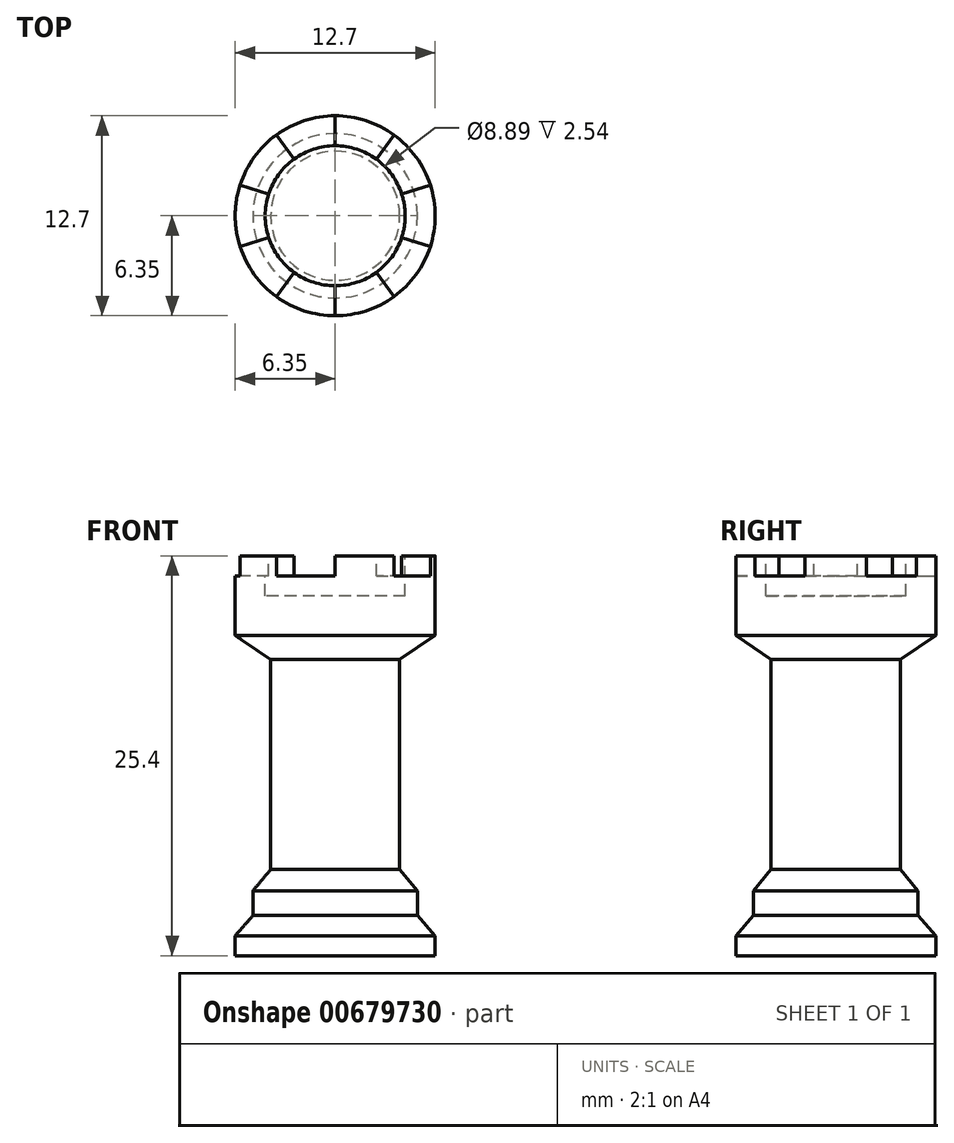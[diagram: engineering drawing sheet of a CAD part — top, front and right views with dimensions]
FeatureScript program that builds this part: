
annotation { "Feature Type Name" : "Feature", "Feature Type Description" : "" }
export const myFeature = defineFeature(function(context is Context, id is Id, definition is map)
    precondition{}
    {
        {
            var Q0;
            Q0=qCreatedBy(makeId("Front.planeOp"),FACE);
            var sketch = newSketch(context, id + "F0", { "sketchPlane" : qUnion([Q0])});
            skLineSegment(sketch, "E0", {"start": v(-6.35, 0) * mm, "end": v(6.35, 0) * mm});
            skLineSegment(sketch, "E1", {"start": v(-6.35, 0) * mm, "end": v(-6.35, 1.27) * mm});
            skLineSegment(sketch, "E2", {"start": v(6.35, 0) * mm, "end": v(6.35, 1.27) * mm});
            skLineSegment(sketch, "E3", {"start": v(-4.1, 3.83) * mm, "end": v(4.1, 3.83) * mm, "construction": true});
            skLineSegment(sketch, "E4", {"start": v(0, 0) * mm, "end": v(0, 25.4) * mm});
            skPoint(sketch, "E5", {"position": v(0, 3.83) * mm});
            skLineSegment(sketch, "E6", {"start": v(-6.35, 25.4) * mm, "end": v(6.35, 25.4) * mm});
            skLineSegment(sketch, "E7", {"start": v(6.35, 25.4) * mm, "end": v(6.35, 20.34) * mm});
            skLineSegment(sketch, "E8", {"start": v(-4.1, 20.34) * mm, "end": v(-4.1, 5.47) * mm});
            skLineSegment(sketch, "E9", {"start": v(4.1, 3.83) * mm, "end": v(4.1, 5.47) * mm, "construction": true});
            skPoint(sketch, "E10", {"position": v(0, 20.34) * mm});
            skLineSegment(sketch, "E11", {"start": v(4.1, 3.83) * mm, "end": v(5.22, 2.55) * mm, "construction": true});
            skLineSegment(sketch, "E12", {"start": v(-4.1, 3.83) * mm, "end": v(-5.22, 2.55) * mm, "construction": true});
            skLineSegment(sketch, "E13", {"start": v(6.35, 20.34) * mm, "end": v(4.1, 18.8) * mm});
            skLineSegment(sketch, "E14", {"start": v(-6.35, 20.34) * mm, "end": v(-4.1, 18.8) * mm});
            skLineSegment(sketch, "E15", {"start": v(-4.1, 18.8) * mm, "end": v(4.1, 18.8) * mm, "construction": true});
            skLineSegment(sketch, "E16", {"start": v(-5.22, 2.55) * mm, "end": v(-5.22, 4.13) * mm});
            skLineSegment(sketch, "E17", {"start": v(5.22, 2.55) * mm, "end": v(5.22, 4.13) * mm});
            skLineSegment(sketch, "E18", {"start": v(5.22, 4.13) * mm, "end": v(4.1, 5.47) * mm});
            skLineSegment(sketch, "E19", {"start": v(-5.22, 4.13) * mm, "end": v(-4.1, 5.47) * mm});
            skLineSegment(sketch, "E20", {"start": v(-4.1, 5.47) * mm, "end": v(4.1, 5.47) * mm, "construction": true});
            skLineSegment(sketch, "E21", {"start": v(-5.22, 4.13) * mm, "end": v(5.22, 4.13) * mm, "construction": true});
            skLineSegment(sketch, "E22", {"start": v(-5.22, 2.55) * mm, "end": v(-6.35, 1.27) * mm});
            skLineSegment(sketch, "E23", {"start": v(5.22, 2.55) * mm, "end": v(6.35, 1.27) * mm});
            skLineSegment(sketch, "E24", {"start": v(-4.1, 5.47) * mm, "end": v(-4.1, 3.83) * mm, "construction": true});
            skLineSegment(sketch, "E25", {"start": v(4.1, 5.47) * mm, "end": v(4.1, 20.34) * mm});
            skLineSegment(sketch, "E26", {"start": v(-6.35, 20.34) * mm, "end": v(6.35, 20.34) * mm, "construction": true});
            skLineSegment(sketch, "E27", {"start": v(-6.35, 20.34) * mm, "end": v(-6.35, 25.4) * mm});
            skSolve(sketch);
        }
        {
            var Q0;
            {var subQ1=sQuery(id+"F0.wireOp",EDGE,"E2");Q0=makeQuery(id+"F0.imprint","IMPRINT",FACE,{"disambiguationData":[TD([[makeQuery(id+"F0.imprint","IMPRINT",EDGE,{"derivedFrom":subQ1}),1.0]])]});}
            var Q1;
            Q1=sQuery(id+"F0.wireOp",EDGE,"E4");
            revolve(context, id + "F1", {"entities" : qUnion([Q0]), "axis" : qUnion([Q1]), "revolveType" : RevolveType.FULL});
        }
        {
            var Q0;
            Q0=makeQuery(id+"F1.opRevolve","SWEPT_FACE",FACE,{"disambiguationData":[OSD([sQuery(id+"F0.wireOp",EDGE,"E6")])]});
            var sketch = newSketch(context, id + "F2", { "sketchPlane" : qUnion([Q0])});
            skCircle(sketch, "E28", {"center": v(0, 0) * mm, "radius": 4.45 * mm});
            skLineSegment(sketch, "E29", {"start": v(0, 4.45) * mm, "end": v(0, 6.35) * mm});
            skLineSegment(sketch, "E30.1.0", {"start": v(-2.61, 3.6) * mm, "end": v(-3.73, 5.14) * mm});
            skLineSegment(sketch, "E30.2.0", {"start": v(-4.23, 1.37) * mm, "end": v(-6.04, 1.96) * mm});
            skLineSegment(sketch, "E30.3.0", {"start": v(-4.23, -1.37) * mm, "end": v(-6.04, -1.96) * mm});
            skLineSegment(sketch, "E30.4.0", {"start": v(-2.61, -3.6) * mm, "end": v(-3.73, -5.14) * mm});
            skLineSegment(sketch, "E30.5.0", {"start": v(0, -4.45) * mm, "end": v(0, -6.35) * mm});
            skLineSegment(sketch, "E30.6.0", {"start": v(2.61, -3.6) * mm, "end": v(3.73, -5.14) * mm});
            skLineSegment(sketch, "E30.7.0", {"start": v(4.23, -1.37) * mm, "end": v(6.04, -1.96) * mm});
            skLineSegment(sketch, "E30.8.0", {"start": v(4.23, 1.37) * mm, "end": v(6.04, 1.96) * mm});
            skLineSegment(sketch, "E30.9.0", {"start": v(2.61, 3.6) * mm, "end": v(3.73, 5.14) * mm});
            skSolve(sketch);
        }
        {
            var Q0;
            {var subQ0=sQuery(id+"F2.wireOp",EDGE,"E28");var subQ5=makeQuery(id+"F2.imprint","INTERSECT",VERTEX,{"derivedFrom":[subQ0,sQuery(id+"F2.wireOp",EDGE,"E30.8.0")]});Q0=makeQuery(id+"F2.imprint","IMPRINT",FACE,{"disambiguationData":[TD([[makeQuery(id+"F2.imprint","IMPRINT",EDGE,{"disambiguationData":[TD([[subQ5,-1.0]])],"derivedFrom":subQ0}),1.0]])]});}
            var Q1;
            {var subQ0=sQuery(id+"F2.wireOp",EDGE,"E29");Q1=makeQuery(id+"F2.imprint","IMPRINT",FACE,{"disambiguationData":[TD([[makeQuery(id+"F2.imprint","IMPRINT",EDGE,{"derivedFrom":subQ0}),1.0]])]});}
            var Q2;
            {var subQ0=sQuery(id+"F2.wireOp",EDGE,"E30.8.0");Q2=makeQuery(id+"F2.imprint","IMPRINT",FACE,{"disambiguationData":[TD([[makeQuery(id+"F2.imprint","IMPRINT",EDGE,{"derivedFrom":subQ0}),1.0]])]});}
            var Q3;
            {var subQ0=sQuery(id+"F2.wireOp",EDGE,"E30.6.0");Q3=makeQuery(id+"F2.imprint","IMPRINT",FACE,{"disambiguationData":[TD([[makeQuery(id+"F2.imprint","IMPRINT",EDGE,{"derivedFrom":subQ0}),1.0]])]});}
            var Q4;
            {var subQ0=sQuery(id+"F2.wireOp",EDGE,"E30.4.0");Q4=makeQuery(id+"F2.imprint","IMPRINT",FACE,{"disambiguationData":[TD([[makeQuery(id+"F2.imprint","IMPRINT",EDGE,{"derivedFrom":subQ0}),1.0]])]});}
            var Q5;
            {var subQ0=sQuery(id+"F2.wireOp",EDGE,"E30.2.0");Q5=makeQuery(id+"F2.imprint","IMPRINT",FACE,{"disambiguationData":[TD([[makeQuery(id+"F2.imprint","IMPRINT",EDGE,{"derivedFrom":subQ0}),1.0]])]});}
            extrude(context, id + "F3", {"entities" : qUnion([Q0, Q1, Q2, Q3, Q4, Q5]), "operationType" : NewBodyOperationType.REMOVE, "oppositeDirection" : true, "depth" : 1.27 * mm, "offsetDistance" : 25.4 * mm});
        }
        {
            var Q0;
            Q0=makeQuery(id+"F3.boolean.opBoolean","COPY",FACE,{"derivedFrom":makeQuery(id+"F3.opExtrude","CAP_FACE",FACE,{"disambiguationData":[OSD([sQuery(id+"F0.wireOp",EDGE,"E6"),sQuery(id+"F0.wireOp",EDGE,"E7"),sQuery(id+"F2.wireOp",EDGE,"E28"),sQuery(id+"F2.wireOp",EDGE,"E29"),sQuery(id+"F2.wireOp",EDGE,"E30.1.0"),sQuery(id+"F2.wireOp",EDGE,"E30.2.0"),sQuery(id+"F2.wireOp",EDGE,"E30.3.0"),sQuery(id+"F2.wireOp",EDGE,"E30.4.0"),sQuery(id+"F2.wireOp",EDGE,"E30.5.0"),sQuery(id+"F2.wireOp",EDGE,"E30.6.0"),sQuery(id+"F2.wireOp",EDGE,"E30.7.0"),sQuery(id+"F2.wireOp",EDGE,"E30.8.0"),sQuery(id+"F2.wireOp",EDGE,"E30.9.0")])],"isStart":false})});
            var sketch = newSketch(context, id + "F4", { "sketchPlane" : qUnion([Q0])});
            skCircle(sketch, "E31", {"center": v(0, 0) * mm, "radius": 4.45 * mm});
            skSolve(sketch);
        }
        {
            var Q0;
            {var subQ0=sQuery(id+"F4.wireOp",EDGE,"E31");var subQ5=makeQuery(id+"F4.imprint","INTERSECT",VERTEX,{"derivedFrom":[makeQuery(id+"F3.boolean.opBoolean","COPY",EDGE,{"derivedFrom":makeQuery(id+"F3.opExtrude","CAP_EDGE",EDGE,{"disambiguationData":[OSD([sQuery(id+"F2.wireOp",EDGE,"E30.8.0")])],"isStart":false})}),subQ0]});Q0=makeQuery(id+"F4.imprint","IMPRINT",FACE,{"disambiguationData":[TD([[makeQuery(id+"F4.imprint","IMPRINT",EDGE,{"disambiguationData":[TD([[subQ5,-1.0]])],"derivedFrom":subQ0}),1.0]])]});}
            extrude(context, id + "F5", {"entities" : qUnion([Q0]), "operationType" : NewBodyOperationType.REMOVE, "oppositeDirection" : true, "depth" : 1.27 * mm, "offsetDistance" : 25.4 * mm});
        }
    });
